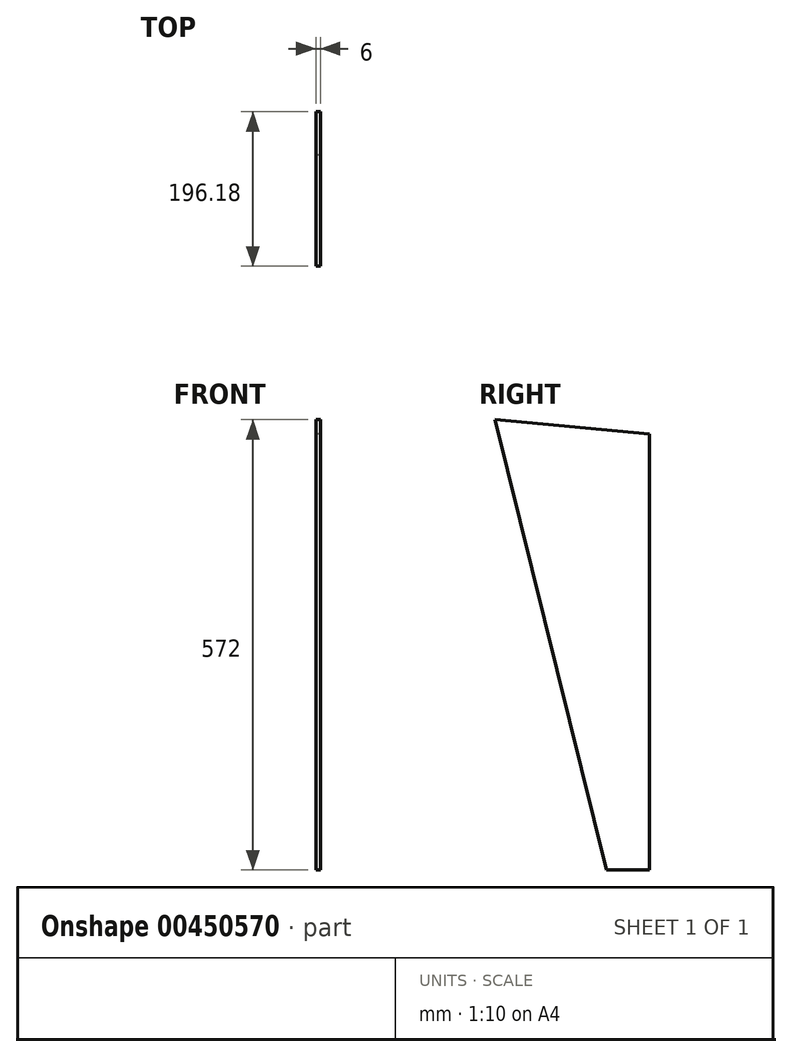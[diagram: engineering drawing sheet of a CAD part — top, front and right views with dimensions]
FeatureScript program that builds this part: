
annotation { "Feature Type Name" : "Feature", "Feature Type Description" : "" }
export const myFeature = defineFeature(function(context is Context, id is Id, definition is map)
    precondition{}
    {
        {
            var Q0;
            Q0=qCreatedBy(makeId("Right.planeOp"),FACE);
            var sketch = newSketch(context, id + "F0", { "sketchPlane" : qUnion([Q0])});
            skLineSegment(sketch, "E0", {"start": v(49.73, 554.76) * mm, "end": v(49.73, 0.76) * mm});
            skLineSegment(sketch, "E1", {"start": v(49.73, 0.76) * mm, "end": v(-5.27, 0.76) * mm});
            skLineSegment(sketch, "E2", {"start": v(49.73, 554.76) * mm, "end": v(-146.45, 572.76) * mm});
            skLineSegment(sketch, "E3", {"start": v(-146.45, 572.76) * mm, "end": v(-5.27, 0.76) * mm});
            skSolve(sketch);
        }
        {
            var Q0;
            Q0=makeQuery(id+"F0.imprint","IMPRINT",FACE,{"disambiguationData":[TD([[makeQuery(id+"F0.imprint","IMPRINT",EDGE,{"derivedFrom":sQuery(id+"F0.wireOp",EDGE,"E0")}),-1.0]])]});
            extrude(context, id + "F1", {"entities" : qUnion([Q0]), "depth" : 6 * mm});
        }
    });
